# Revit family: NBS_Senator_OffcChrs_Freeflex
name_source: partatom
category: Furniture
revit_build: Autodesk Revit 2016 (Build: 20151007_0715(x64)
units: mm (PartAtom-declared; Revit-internal decimal feet)

## family parameters
Always vertical = Yes
Cut with Voids When Loaded = No
Room Calculation Point = No
Shared = No
Work Plane-Based = No

## types (2) — shared parameters
Adjustability = Up to 22° of recline motion, back lock, seat depth, height adjustable, multi-adjustable arms
AssetType = Moveable
BaseFinishes = Graphite plastic, polished aluminium
Category = Pr_40_50_12_57:Office chairs
CodePerformance = ANSI/BIFMA X5.1-2011
Depth = 460 mm  [stored 1.50919 ft]
DurationUnit = year
ExpectedLife = 10
FinishOptions = Plastic components available in graphite with black or light grey back and arms, can be upholstered in a broad range of contract upholstery fabrics, vinyls and leathers from senator standard upholstery collection
FootHeight = 5 mm  [stored 0.0164042 ft]
FrameMountingMaterial = NBS_Concept
HighestSeatingHeight = 565 mm
IfcExportAs = IfcFurnitureType
IfcExportType = CHAIR
IsBuiltIn = No
LegHeight = 377 mm  [stored 1.23688 ft]
LowestSeatingHeight = 450 mm  [stored 1.47638 ft]
ManufacturerName = Senator
ManufacturerURL = www.senator.co.uk
MeshSidePanelColours = Fog, carbon, storm, sunset, aqua, avocado
NBSCertification = www.nationalbimlibrary.com/cert/43nczsid
NBSDescription = Office chairs
NBSReference = 45-35-20/330
NominalDepth = 690 mm
NominalLength = 690 mm
NominalWidth = 690 mm
OfficeChairBase = NBS_TheSenatorGroup_OfficeChairs_Freeflex-5StarBaseWCastors
OfficeChairMechanism = NBS_TheSenatorGroup_OfficeChairs_Freeflex_TiltMechanism
OfficeChairSeat = NBS_TheSenatorGroup_OfficeChairs_Freeflex_Seat
ProductInformation = www.thesenatorgroup.com/FamilyDocuments/711/Senator_SPEC_2015_V2_Freeflex_Visitor.pdf
SeatArmMaterial = NBS_Concept
SeatBaseMaterial = NBS_Concept
SeatFrameMaterial = NBS_Concept
SeatTiltMaterial = NBS_Concept
SeatTrimMaterial = NBS_Concept
SeatingHeight = 507 mm  [stored 1.66339 ft]
SeatingSeatMaterial = NBS_Concept
SeatsAndBacksColourOptions = Fog, carbon, storm, sunset, aqua, avocado, brushed
Size = 690 x 690 x 995 mm
StandardsDimensions = ANSI/BIFMA X5.1-2011
StandardsDurability = ANSI/BIFMA X5.1-2011
StandardsSafetyRequirements = ANSI/BIFMA X5.1-2011
Status = UNSET
SustainabilityPerformance = 100% recycleable
Uniclass2015Code = Pr_40_50_12_57
Uniclass2015Title = Office chairs
Uniclass2015Version = Products v1.9
Version = 1
WarrantyDescription = Senator warrants that its manufactured products are free from defects for a period of ten years on Senator seating ranges
WarrantyDurationParts = 10
WarrantyDurationUnit = year
Width = 524 mm  [stored 1.71916 ft]
zero-valued in all types: NominalHeight

## per-type parameters (varying)
| type | BIMObjectName | Description | Features | HasArms | ModelReference | Name |
| FLX740 | NBS_Senator_OfficeChairs_Freeflex_FLX740 | Task chair with no arms | 65 mm hard wheel castors, graphite gas lift - 150 kg,  weight controlled synchronised mechanism with travel limitation in 4 steps including locking upright, Integrated flexible back membrane, moulded seat and back foam, user instructions | No | Freeflex | OfficeChairs_Freeflex_FLX740_Senator |
| FLX740HA | NBS_Senator_OfficeChairs_Freeflex_FLX740HA | Task chair with heiaght and width adjustable arms | 65 mm hard wheel castors, graphite gas lift - 150 kg, weight controlled synchronised mechanism with travel limitation in 4 steps including locking upright, Integrated flexible back membrane, height and width adjustable arms, moulded seat and back foam, user instructions | Yes | Freeflex with arms | OfficeChairs_Freeflex_FLX740HA_Senator |

note: column(s) folded — value = type name in every type: ModelNumber

note: [stored X ft] marks values corroborated as IEEE doubles in the binary element streams (Revit-internal decimal feet)

## geometry (parser evidence)
native form markers: Sweep x14
no freeform markers — native parametric forms only
